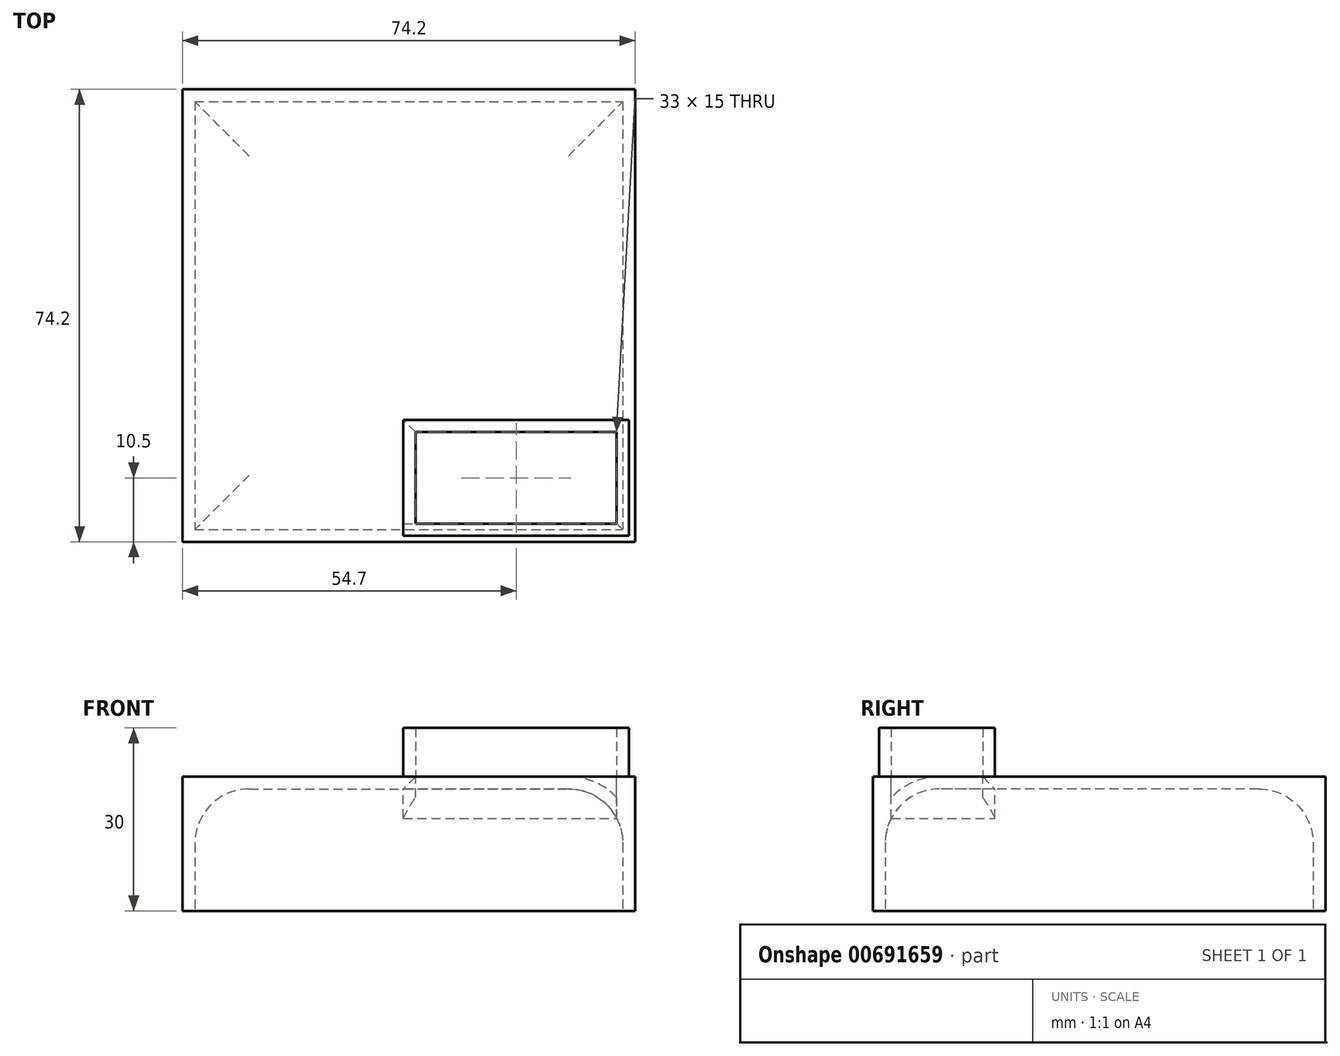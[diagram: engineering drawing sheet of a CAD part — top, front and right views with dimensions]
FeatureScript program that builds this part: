
annotation { "Feature Type Name" : "Feature", "Feature Type Description" : "" }
export const myFeature = defineFeature(function(context is Context, id is Id, definition is map)
    precondition{}
    {
        {
            var Q0;
            Q0=qCreatedBy(makeId("Top.planeOp"),FACE);
            var sketch = newSketch(context, id + "F0", { "sketchPlane" : qUnion([Q0])});
            skLineSegment(sketch, "E0.bottom", {"start": v(-35.1, 35.1) * mm, "end": v(35.1, 35.1) * mm});
            skLineSegment(sketch, "E0.top", {"start": v(-35.1, -35.1) * mm, "end": v(35.1, -35.1) * mm});
            skLineSegment(sketch, "E0.left", {"start": v(-35.1, 35.1) * mm, "end": v(-35.1, -35.1) * mm});
            skLineSegment(sketch, "E0.right", {"start": v(35.1, 35.1) * mm, "end": v(35.1, -35.1) * mm});
            skSolve(sketch);
        }
        {
            var Q0;
            Q0=makeQuery(id+"F0.imprint","IMPRINT",FACE,{"disambiguationData":[TD([[makeQuery(id+"F0.imprint","IMPRINT",EDGE,{"derivedFrom":sQuery(id+"F0.wireOp",EDGE,"E0.bottom")}),-1.0]])]});
            extrude(context, id + "F1", {"entities" : qUnion([Q0]), "depth" : 20 * mm, "offsetDistance" : 25 * mm});
        }
        {
            var Q0;
            Q0=makeQuery(id+"F1.opExtrude","CAP_FACE",FACE,{"disambiguationData":[OSD([sQuery(id+"F0.wireOp",EDGE,"E0.bottom"),sQuery(id+"F0.wireOp",EDGE,"E0.top"),sQuery(id+"F0.wireOp",EDGE,"E0.left"),sQuery(id+"F0.wireOp",EDGE,"E0.right")])],"isStart":true});
            shell(context, id + "F2", {"entities" : qUnion([Q0]), "thickness" : 2 * mm, "oppositeDirection" : true});
        }
        {
            var Q0;
            Q0=makeQuery(id+"F1.opExtrude","CAP_FACE",FACE,{"disambiguationData":[OSD([sQuery(id+"F0.wireOp",EDGE,"E0.bottom"),sQuery(id+"F0.wireOp",EDGE,"E0.top"),sQuery(id+"F0.wireOp",EDGE,"E0.left"),sQuery(id+"F0.wireOp",EDGE,"E0.right")])],"isStart":false});
            var sketch = newSketch(context, id + "F3", { "sketchPlane" : qUnion([Q0])});
            skLineSegment(sketch, "E1.bottom", {"start": v(1.1, -19.1) * mm, "end": v(34.1, -19.1) * mm});
            skLineSegment(sketch, "E1.top", {"start": v(1.1, -34.1) * mm, "end": v(34.1, -34.1) * mm});
            skLineSegment(sketch, "E1.left", {"start": v(1.1, -19.1) * mm, "end": v(1.1, -34.1) * mm});
            skLineSegment(sketch, "E1.right", {"start": v(34.1, -19.1) * mm, "end": v(34.1, -34.1) * mm});
            skSolve(sketch);
        }
        {
            var Q0;
            Q0=makeQuery(id+"F3.imprint","IMPRINT",FACE,{"disambiguationData":[TD([[makeQuery(id+"F3.imprint","IMPRINT",EDGE,{"derivedFrom":sQuery(id+"F3.wireOp",EDGE,"E1.bottom")}),-1.0]])]});
            extrude(context, id + "F4", {"entities" : qUnion([Q0]), "operationType" : NewBodyOperationType.REMOVE, "oppositeDirection" : true, "depth" : 25 * mm, "offsetDistance" : 25 * mm});
        }
        {
            var Q0;
            Q0=makeQuery(id+"F3.imprint","IMPRINT",FACE,{"disambiguationData":[TD([[makeQuery(id+"F3.imprint","IMPRINT",EDGE,{"derivedFrom":sQuery(id+"F3.wireOp",EDGE,"E1.bottom")}),-1.0]])]});
            extrude(context, id + "F5", {"entities" : qUnion([Q0]), "depth" : 25 * mm, "offsetDistance" : 25 * mm});
        }
        {
            var Q0;
            Q0=makeQuery(id+"F5.opExtrude","CAP_FACE",FACE,{"disambiguationData":[OSD([sQuery(id+"F3.wireOp",EDGE,"E1.bottom"),sQuery(id+"F3.wireOp",EDGE,"E1.top"),sQuery(id+"F3.wireOp",EDGE,"E1.left"),sQuery(id+"F3.wireOp",EDGE,"E1.right")])],"isStart":true});
            shell(context, id + "F6", {"entities" : qUnion([Q0]), "thickness" : 2 * mm, "oppositeDirection" : true});
        }
        {
            var Q0;
            Q0=makeQuery(id+"F5.opExtrude","SWEPT_FACE",FACE,{"disambiguationData":[OSD([sQuery(id+"F3.wireOp",EDGE,"E1.top")])]});
            var sketch = newSketch(context, id + "F7", { "sketchPlane" : qUnion([Q0])});
            skLineSegment(sketch, "E2.bottom", {"start": v(-0.9, 22) * mm, "end": v(36.1, 22) * mm});
            skLineSegment(sketch, "E2.top", {"start": v(-0.9, 49) * mm, "end": v(36.1, 49) * mm});
            skLineSegment(sketch, "E2.left", {"start": v(-0.9, 22) * mm, "end": v(-0.9, 49) * mm});
            skLineSegment(sketch, "E2.right", {"start": v(36.1, 22) * mm, "end": v(36.1, 49) * mm});
            skLineSegment(sketch, "E3.bottom", {"start": v(-0.9, 36.93) * mm, "end": v(36.1, 36.93) * mm});
            skLineSegment(sketch, "E3.top", {"start": v(-0.9, 30) * mm, "end": v(36.1, 30) * mm});
            skLineSegment(sketch, "E3.left", {"start": v(-0.9, 36.93) * mm, "end": v(-0.9, 30) * mm});
            skLineSegment(sketch, "E3.right", {"start": v(36.1, 36.93) * mm, "end": v(36.1, 30) * mm});
            skSolve(sketch);
        }
        {
            var Q0;
            Q0=makeQuery(id+"F7.imprint","IMPRINT",FACE,{"disambiguationData":[TD([[makeQuery(id+"F7.imprint","IMPRINT",EDGE,{"derivedFrom":sQuery(id+"F7.wireOp",EDGE,"E3.bottom")}),-1.0]])]});
            var Q1;
            {var subQ0=sQuery(id+"F7.wireOp",EDGE,"E2.top");Q1=makeQuery(id+"F7.imprint","IMPRINT",FACE,{"disambiguationData":[TD([[makeQuery(id+"F7.imprint","IMPRINT",EDGE,{"derivedFrom":subQ0}),-1.0]])]});}
            extrude(context, id + "F8", {"entities" : qUnion([Q0, Q1]), "operationType" : NewBodyOperationType.REMOVE, "oppositeDirection" : true, "depth" : 25 * mm, "offsetDistance" : 25 * mm});
        }
        {
            var Q0;
            {var subQ0=sQuery(id+"F0.wireOp",EDGE,"E0.left");Q0=makeQuery(id+"F2.opShell","OFFSET_EDGE",EDGE,{"disambiguationData":[OSD([subQ0]),TDD([makeQuery(id+"F1.opExtrude","CAP_EDGE",EDGE,{"disambiguationData":[OSD([subQ0])],"isStart":false})])]});}
            var Q1;
            {var subQ0=sQuery(id+"F0.wireOp",EDGE,"E0.bottom");Q1=makeQuery(id+"F2.opShell","OFFSET_EDGE",EDGE,{"disambiguationData":[OSD([subQ0]),TDD([makeQuery(id+"F1.opExtrude","CAP_EDGE",EDGE,{"disambiguationData":[OSD([subQ0])],"isStart":false})])]});}
            var Q2;
            {var subQ0=sQuery(id+"F0.wireOp",EDGE,"E0.right");Q2=makeQuery(id+"F2.opShell","OFFSET_EDGE",EDGE,{"disambiguationData":[OSD([subQ0]),TDD([makeQuery(id+"F1.opExtrude","CAP_EDGE",EDGE,{"disambiguationData":[OSD([subQ0])],"isStart":false})])]});}
            var Q3;
            {var subQ0=sQuery(id+"F0.wireOp",EDGE,"E0.top");Q3=makeQuery(id+"F2.opShell","OFFSET_EDGE",EDGE,{"disambiguationData":[OSD([subQ0]),TDD([makeQuery(id+"F1.opExtrude","CAP_EDGE",EDGE,{"disambiguationData":[OSD([subQ0])],"isStart":false})])]});}
            fillet(context, id + "F9", {"entities" : qUnion([Q0, Q1, Q2, Q3]), "radius" : 8.93 * mm, "tangentPropagation" : true, "allowEdgeOverflow" : false});
        }
        {
            var Q0;
            Q0=makeQuery(id+"F4.boolean.opBoolean","INTERSECT",EDGE,{"derivedFrom":[makeQuery(id+"F2.opShell","OFFSET_FACE",FACE,{"disambiguationData":[OSD([sQuery(id+"F0.wireOp",EDGE,"E0.bottom"),sQuery(id+"F0.wireOp",EDGE,"E0.top"),sQuery(id+"F0.wireOp",EDGE,"E0.left"),sQuery(id+"F0.wireOp",EDGE,"E0.right")])]}),makeQuery(id+"F4.opExtrude","SWEPT_FACE",FACE,{"disambiguationData":[OSD([sQuery(id+"F3.wireOp",EDGE,"E1.bottom")])]})]});
            var Q1;
            Q1=makeQuery(id+"F4.boolean.opBoolean","INTERSECT",EDGE,{"derivedFrom":[makeQuery(id+"F2.opShell","OFFSET_FACE",FACE,{"disambiguationData":[OSD([sQuery(id+"F0.wireOp",EDGE,"E0.bottom"),sQuery(id+"F0.wireOp",EDGE,"E0.top"),sQuery(id+"F0.wireOp",EDGE,"E0.left"),sQuery(id+"F0.wireOp",EDGE,"E0.right")])]}),makeQuery(id+"F4.opExtrude","SWEPT_FACE",FACE,{"disambiguationData":[OSD([sQuery(id+"F3.wireOp",EDGE,"E1.left")])]})]});
            chamfer(context, id + "F10", {"entities" : qUnion([Q0, Q1]), "width" : 2 * mm, "tangentPropagation" : true});
        }
    });
